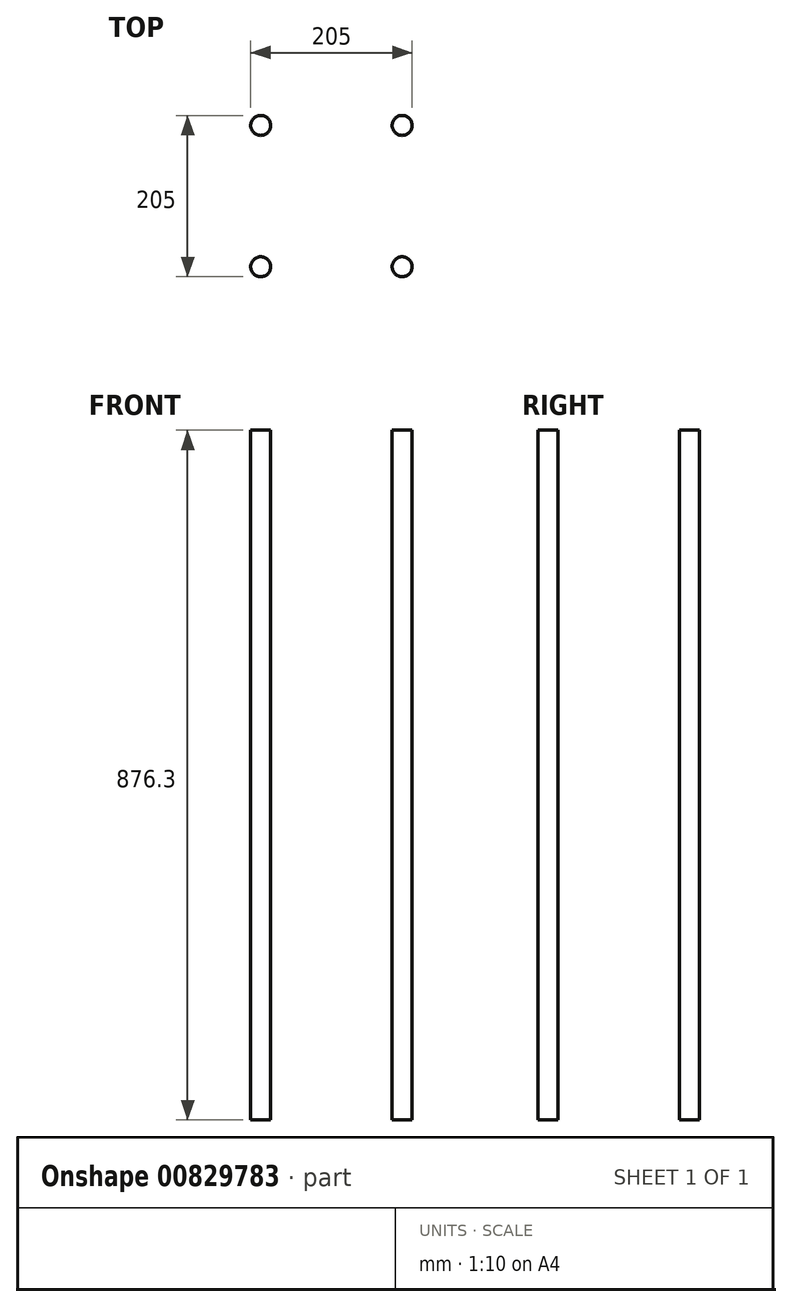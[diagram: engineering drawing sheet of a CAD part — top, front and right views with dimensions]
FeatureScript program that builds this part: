
annotation { "Feature Type Name" : "Feature", "Feature Type Description" : "" }
export const myFeature = defineFeature(function(context is Context, id is Id, definition is map)
    precondition{}
    {
        {
            var Q0;
            Q0=qCreatedBy(makeId("Top.planeOp"),FACE);
            var sketch = newSketch(context, id + "F0", { "sketchPlane" : qUnion([Q0])});
            skLineSegment(sketch, "E0.bottom", {"start": v(89.8, 89.8) * mm, "end": v(-89.8, 89.8) * mm, "construction": true});
            skLineSegment(sketch, "E0.top", {"start": v(89.8, -89.8) * mm, "end": v(-89.8, -89.8) * mm, "construction": true});
            skLineSegment(sketch, "E0.left", {"start": v(89.8, 89.8) * mm, "end": v(89.8, -89.8) * mm, "construction": true});
            skLineSegment(sketch, "E0.right", {"start": v(-89.8, 89.8) * mm, "end": v(-89.8, -89.8) * mm, "construction": true});
            skPoint(sketch, "E0.middle", {"position": v(0, 0) * mm});
            skCircle(sketch, "E1", {"center": v(-89.8, 89.8) * mm, "radius": 12.7 * mm});
            skCircle(sketch, "E2", {"center": v(89.8, 89.8) * mm, "radius": 12.7 * mm});
            skCircle(sketch, "E3", {"center": v(89.8, -89.8) * mm, "radius": 12.7 * mm});
            skCircle(sketch, "E4", {"center": v(-89.8, -89.8) * mm, "radius": 12.7 * mm});
            skCircle(sketch, "E5", {"center": v(0, 0) * mm, "radius": 139.7 * mm, "construction": true});
            skSolve(sketch);
        }
        {
            var Q0;
            Q0 = qSketchRegion(id + "F0", true);
            extrude(context, id + "F1", {"entities" : qUnion([Q0]), "depth" : 876.3 * mm, "offsetDistance" : 25.4 * mm});
        }
    });
